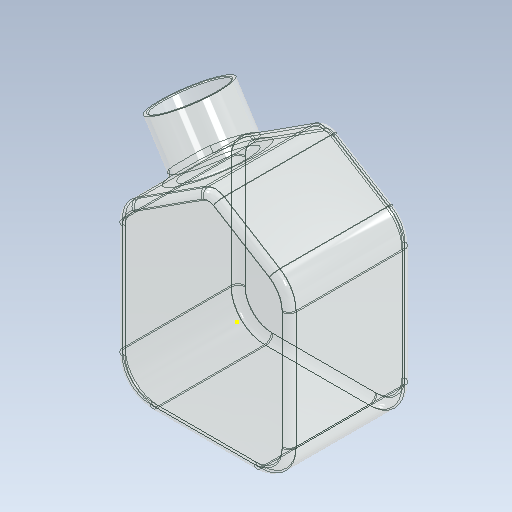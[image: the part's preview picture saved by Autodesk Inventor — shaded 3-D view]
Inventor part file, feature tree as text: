
AUTODESK INVENTOR PART (.ipt)
format: ipt  version: 2020 (Build 240168000, 168)  size: 340,480 bytes
history: native  units: in
note: dims shown in document units (in); Inventor stores cm internally (conversion verified against a paired STEP export)
features: sketch x7, fillet x5, extrude x4, plane x2, projected_geometry x2, sweep x1, chamfer x1
ambient origin geometry x8: Origin, YZ Plane, XZ Plane, XY Plane, X Axis, Y Axis, Z Axis, Center Point
bodies: Solid1 (feature_tree)
feature tree (22):
  sketch  "Sketch1"  dims[d0=3.937in d1=5.0394in]
  sketch  "Sketch2"  dims[d2=3.8976in d3=3.7008in d4=2.0866in d5=0.7874in]
  plane  "Work Plane1"
  sweep  "Sweep1"
  extrude  "Extrusion1"  Depth=3.7008in
  fillet  "Fillet2"  Radius=2.0866in
  fillet  "Fillet3"  Radius=0.7874in
  extrude  "Extrusion2"  Depth=0.3937in
  plane  "Work Plane3"
  fillet  "Fillet4"  Radius=0.6693in
  fillet  "Fillet5"  Radius=0.3937in
  extrude  "Extrusion3"  Depth=2.7165in
  fillet  "Fillet6"  Radius=0.0315in
  chamfer  "Chamfer1"  [1 undecoded]
  extrude  "Extrusion4"  Depth=0.1575in
  sketch  "Sketch3"  dims[d6=0.7874in d7=0.7874in d8=0.6693in d9=0.3937in]
  sketch  "Sketch4"  dims[d10=2.125in d11=2.7165in d12=0.0315in]
  projected_geometry  "Projected Loop1"
  sketch  "Sketch5"  dims[d13=0.0in d14=0.0in d15=0.0in]
  projected_geometry  "Projected Loop2"
  sketch  "Sketch6"  dims[d16=0.0315in d17=0.0in d19=0.1575in]
  sketch  "Sketch7"  dims[d20=0.1575in d21=0.0315in d22=0.0in d23=-1.125in d24=0.1575in d25=0.1575in d26=0.7874in d27=1.4567in d28=1.6142in d29=1.1811in d30=0.0315in d31=0.0in d32=0.0in d33=0.1575in d34=0.0197in d35=0.0787in d36=45.0deg d37=1.1811in d38=0.0in]
note: 1 required parameter value undecoded (feature->parameter linkage not recoverable at this tier; creation-order binding heuristic only, values carry confidence <= 0.55)
